# Revit family: Doors-Sliding_WON-DOOR_FireGuard-Straight_Flat-Lead-Post - Test V1 - all heights
name_source: partatom
category: Doors
units: mm (PartAtom-declared; Revit-internal decimal feet)

## family parameters
Always vertical = Yes
Cut with Voids When Loaded = No
Host = Wall
OmniClass Number = 23.30.10.21.11
OmniClass Title = Fire Doors
Room Calculation Point = No
Shared = No

## types (4) — shared parameters
Description = The Won-Door SteelGuard doors with flat lead posts are specifically designed for straight, single parting applications that are up to 40 feet wide and up to 12 feet in height.
Door Finish = Won-Door-Metal-Platinum
Manufacturer = Won-Door Corporation
Model = SteelGuard Straight With Flat Lead Post
Product Page URL = https://www.wondoor.com
Product data url = https://bimobject.com
Rod Position Depth = 1' - 0"
Thickness = 1' - 6"
URL = https://www.wondoor.com
Version = 1
Wall Closure = By host

## per-type parameters (varying)
| type | Fire Rating | Offset for Backing Depth | Offset for Backing Width | Offset for Stack Depth | Pocket Thickness |
| Non Rated | Non Rated | 0' - 6 1/8" | 0' - 3 1/8" | 0' - 4 7/8" | 2' - 3 3/4" |
| 20/60 Minute | 60 Minute Fire Rating | 0' - 6 1/8" | 0' - 3 1/8" | 0' - 4 7/8" | 2' - 3 3/4" |
| 90 Minute | 90 Minute Fire Rating | 0' - 7 3/8" | 0' - 3 1/4" | 0' - 6 1/8" | 2' - 6 1/4" |
| 180 Minute | 180 Minute Fire Rating | 0' - 8 5/8" | 0' - 3 1/4" | 0' - 7 3/8" | 2' - 8 3/4" |

## geometry (parser evidence)
native form markers: Sweep x6
no freeform markers — native parametric forms only
